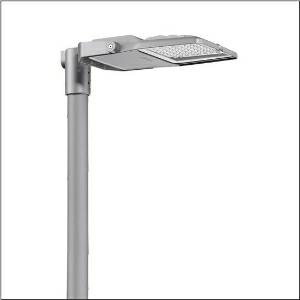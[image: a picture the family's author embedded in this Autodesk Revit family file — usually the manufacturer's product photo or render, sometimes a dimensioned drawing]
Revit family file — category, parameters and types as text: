
# Revit family: floodlight_fl_21_mini___pl64_5xa7776d4e3a_3ee3
name_source: partatom
category: Lighting Fixtures
units: mm (PartAtom-declared; Revit-internal decimal feet)

## family parameters
Cut with Voids When Loaded = No
Host = Face
Light Source = No
Part Type = Normal
Room Calculation Point = No
Round Connector Dimension = Use Diameter
Shared = No

## types (1)
- --- (1 x LED, 17960 lm, 142.9 W, 4000K)
    Apparent Load = 143 VA
    CIE Flux Codes = 28 80 98 100 100
    Color Rendering = 70
    Color Temperature = 4000K
    Default Elevation = 1800 mm
    Description = Floodlight FL 21 mini, floodlight, primary light control with lens, of PMMA, primary optical cover: protective disc, of toughened safety glass, transparent, light distribution: PL64, light emission: direct distribution, installation type: surface-mounted, LED, High Power LED, rated luminous flux: 17.960lm, luminous efficacy: 126lm/W, light colour: 740, colour temperature: 4000K, control gear: D4iSmart Interface (Zhaga), control: overheat protection, constant luminous flux control, time-dependent luminous flux control, flexible luminous flux parameterisation, pre-setting: logarithmic dimming characteristic, with terminal, 6-pole, mains connection: 220..240V, AC, 50/60Hz, start of lifetime: 143W, end of service life: 151W, reduction: 63W, mast bracket, of diecast aluminium, powder-coated, Siteco® metallic grey (DB 702S), corrosivity category C5 mid according to DIN EN ISO 12944, suitable for swimming pools, chlorine-resistant, sealing non-destructively replaceable, mast bracket, of steel, galvanised, powder-coated, Siteco® metallic grey (DB 702S), Smart Interface below and above, protection rating (complete): IP66, insulation class (complete): insulation class II (safety insulation), certification: CE, ENEC, VDE, protection symbol: D, impact resistance: IK08, permissible operating ambient temperature: -40..+40°C, permissible operating ambient temperature for outdoor applications: -40..+50°C, standard: DIN EN 12944, LABS conformity tested according to VDMA 24364:2018-05, packaging unit: 1 piece

Light Distribution: PL64
    Height = 70 mm
    Lamp = 1 x LED
    Lamp Light Flux = 17960 lm
    Lamp Power = 142.9 W
    Lamp count = 1
    Length = 485 mm
    Luminous efficacy = 126 lm/W
    Manufacturer = Siteco
    ModVariant = No
    Model = 5XA7776D4E3A
    Number of Poles = 1
    OnlyDefault = Yes
    Power Factor = 1
    Product Name = Floodlight FL 21 mini | PL64
    Product group = floodlight | pylon annexe
    ProductGroupID = 6200
    Protection Class = Protection class II
    Protection Degree = IP 66
    RLX_Detail_Level = 1
    RLX_Emergency_Light_Flux = 0 lm
    RLX_Emergency_Type = 0
    RLX_Emergency_Type_DB = No
    RlxData = <blob elided: 101341 chars, md5=fea6cd09>
    Socket = socket
    Standby Power = 0 W
    System Light Flux = 17960 lm
    System Power = 143 W
    Type Comments = factory setting: luminous flux: 100 % | dim-lin: 254 | 730 mA
    Type Image = l_1007125.jpg
    URL = http://relux.com
    VarID = @adj_097016
    Voltage = 0 V
    Weight = 0.00 kg
    Width = 337 mm

## geometry (parser evidence)
native form markers: Blend x4, Sweep x11
no freeform markers — native parametric forms only
